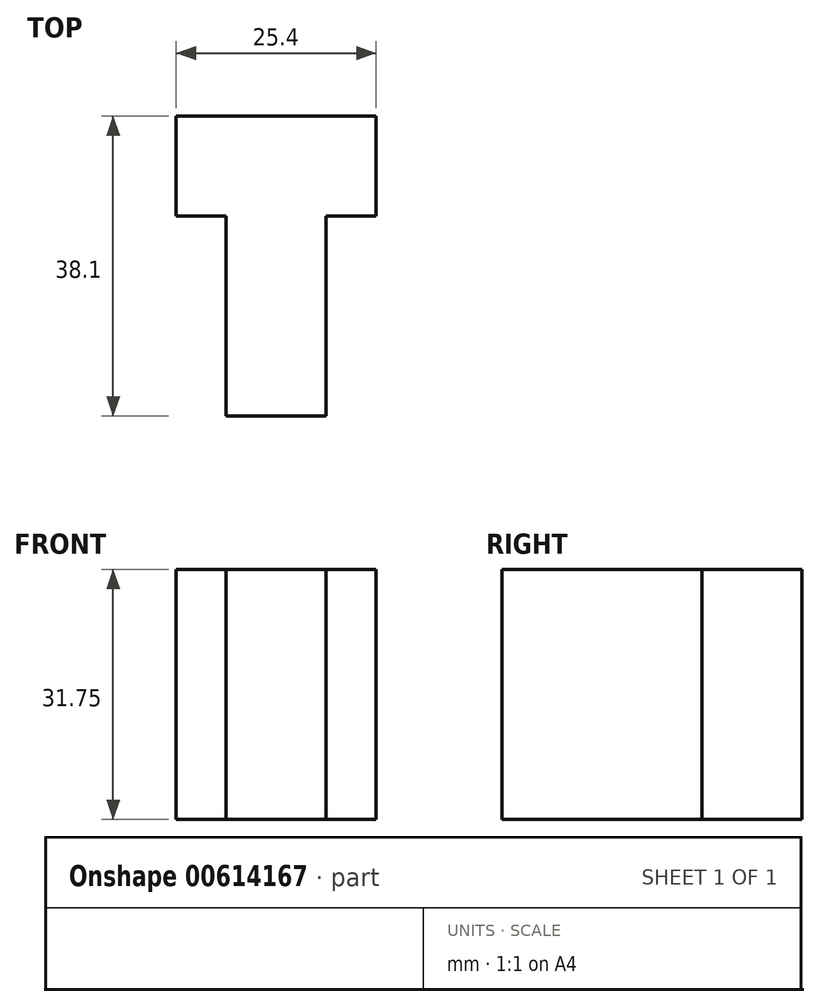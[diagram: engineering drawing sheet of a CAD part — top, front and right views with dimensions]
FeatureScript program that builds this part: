
annotation { "Feature Type Name" : "Feature", "Feature Type Description" : "" }
export const myFeature = defineFeature(function(context is Context, id is Id, definition is map)
    precondition{}
    {
        {
            var Q0;
            Q0=qCreatedBy(makeId("Top.planeOp"),FACE);
            var sketch = newSketch(context, id + "F0", { "sketchPlane" : qUnion([Q0])});
            skLineSegment(sketch, "E0", {"start": v(-6.35, 3.26) * mm, "end": v(-6.35, -9.44) * mm});
            skLineSegment(sketch, "E1", {"start": v(-6.35, -9.44) * mm, "end": v(0, -9.44) * mm});
            skLineSegment(sketch, "E2", {"start": v(-6.35, 3.26) * mm, "end": v(19.05, 3.26) * mm});
            skLineSegment(sketch, "E3", {"start": v(19.05, 3.26) * mm, "end": v(19.05, -9.44) * mm});
            skLineSegment(sketch, "E4", {"start": v(19.05, -9.44) * mm, "end": v(12.7, -9.44) * mm});
            skLineSegment(sketch, "E5", {"start": v(12.7, -9.44) * mm, "end": v(12.7, -34.84) * mm});
            skLineSegment(sketch, "E6", {"start": v(12.7, -34.84) * mm, "end": v(0, -34.84) * mm});
            skLineSegment(sketch, "E7", {"start": v(0, -9.44) * mm, "end": v(0, -34.84) * mm});
            skSolve(sketch);
        }
        {
            var Q0;
            Q0 = qSketchRegion(id + "F0", true);
            extrude(context, id + "F1", {"entities" : qUnion([Q0]), "depth" : 31.75 * mm, "offsetDistance" : 25.4 * mm});
        }
    });
